# Revit family: Skylight_SF_AmericanSkylites
name_source: partatom
category: Windows
units: mm (PartAtom-declared; Revit-internal decimal feet)

## family parameters
Always vertical = No
Cut with Voids When Loaded = No
Host = Roof
Room Calculation Point = No
Shared = No

## types (61) — shared parameters
Assembly Code = B3020110
Building Codes = http://www.americanskylites.com
Construction Details = http://www.arcat.com
E283_Air Infiltration = 898560.00 psf
E330_Uniform Load_Neg = 10800000.00 psf
E330_Uniform Load_Pos = 9936000.00 psf
E547_E331_Water Penetration = 2160000.00 psf
ENERGYSTAR Qualified = Non-Compliant
Expected Lifespan (Years) = 20
Flange Extension = 0' - 3"
Flashing Clearance = 0' - 0 3/8"
Green Building-LEED = http://www.arcat.com
Installation Phase = Roof Enclosure
Insulation Thickness = 0' - 0 3/4"
Keynote = 08620
Maintenance Schedule (Months) = 12
Manufacturer = American Skylights, Inc
Manufacturer Fax = 817-633-4616
Manufacturer Website = http://www.americanskylites.com
Operation = Fixed
Product Data = http://www.arcat.com
Product Properties = http://www.arcat.com
Sales Information = http://www.americanskylites.com
Send Message = http://admin.arcat.com
SpecWizard = http://www.arcat.com
Specification = http://www.arcat.com
Warranty Duration (Years) = 10
zero-valued in all types: Cost

## per-type parameters (varying)
| type | Description | Dome Type | Frame Material | Inner Dome Material | Insulation Material | IsInsulated | Model | Outer Dome Material | SHGC | Type Comments | U_Factor | Unit Height |
| Miami-Dade Approved Thermally Broken Curb Mount - Glazing and size as Specified | CM4669 Single Dome Skylight - Glazing As Specified | Glazing_Double Dome : As Specified | Aluminum 0.060" - Finish as Specified | None | Wood Materials - Pine | No | CM4669 | Acrylic - Clear | 1.1155 |  | 0.8 | 0' - 9" |
| Thermally Broken Fall Protection - Glazing and size as Specified | Thermally Broken Double Dome Skylight - Size and Glazing As Specified | Glazing_Double Dome : As Specified | Aluminum 0.060" - Finish as Specified | Polycarbonate - Clear | Wood Materials - Pine | Yes | TCM-FG | Polycarbonate - Clear | 1.023 | Report# CCLI-00-109 | 0.5 | 1' - 0" |
| Thermally Broken Venting Flat - Glazing and size as Specified | Thermally Broken Venting Flat Skylight - Size and Glazing As Specified | Glazing_Double Dome : As Specified | Aluminum 0.060" - Finish as Specified | None | Wood Materials - Pine | Yes | GTVCM | Twinwall Polycarbonate - Clear | 1.1155 |  | 0.8 | 1' - 0" |
| Thermally Broken Venting Double Dome - Glazing and size as Specified | Thermally Broken Venting Double Dome Skylight - Size and Glazing As Specified | Glazing_Double Dome : As Specified | Aluminum 0.060" - Finish as Specified | Acrylic - Clear | Wood Materials - Pine | Yes | TVCM | Acrylic - Clear | 1.023 |  | 0.5 | 1' - 0" |
| Thermally Broken Venting Dome - Glazing and size as Specified | Thermally Broken Venting Dome Skylight - Size and Glazing As Specified | Glazing_Double Dome : As Specified | Aluminum 0.060" - Finish as Specified | None | Wood Materials - Pine | Yes | TVCM | Acrylic - Clear | 1.1155 |  | 0.8 | 1' - 0" |
| Thermally Broken 40 Deg Double Pyramid - Glazing and size as Specified | Thermally Broken 40 Deg Double Pyramid Skylight - Size and Glazing As Specified | Glazing_Double Dome : As Specified | Aluminum 0.060" - Finish as Specified | Acrylic - Clear | Wood Materials - Pine | Yes | TCM-PYR | Acrylic - Clear | 1.023 |  | 0.5 | 1' - 0" |
| Thermally Broken 40 Deg Pyramid - Glazing and size as Specified | Thermally Broken 40 Deg Pyramid Skylight - Size and Glazing As Specified | Glazing_Double Dome : As Specified | Aluminum 0.060" - Finish as Specified | None | Wood Materials - Pine | Yes | TCM-PYR | Acrylic - Clear | 1.1155 |  | 0.8 | 1' - 0" |
| Thermally Broken 30 Deg Double Pyramid - Glazing and size as Specified | Thermally Broken 30 Deg Double Pyramid Skylight - Size and Glazing As Specified | Glazing_Double Dome : As Specified | Aluminum 0.060" - Finish as Specified | Acrylic - Clear | Wood Materials - Pine | Yes | TCM-PYR | Acrylic - Clear | 1.023 |  | 0.5 | 1' - 0" |
| Thermally Broken 30 Deg Pyramid - Glazing and size as Specified | Thermally Broken 30 Deg Pyramid Skylight - Size and Glazing As Specified | Glazing_Double Dome : As Specified | Aluminum 0.060" - Finish as Specified | None | Wood Materials - Pine | Yes | TCM-PYR | Acrylic - Clear | 1.1155 |  | 0.8 | 1' - 0" |
| Thermally Broken 22 Deg Double Pyramid - Glazing and size as Specified | Thermally Broken 22 Deg Double Pyramid Skylight - Size and Glazing As Specified | Glazing_Double Dome : As Specified | Aluminum 0.060" - Finish as Specified | Acrylic - Clear | Wood Materials - Pine | Yes | TCM-PYR | Acrylic - Clear | 1.023 |  | 0.5 | 1' - 0" |
| Thermally Broken 22 Deg Pyramid - Glazing and size as Specified | Thermally Broken 22 Deg Pyramid Skylight - Size and Glazing As Specified | Glazing_Double Dome : As Specified | Aluminum 0.060" - Finish as Specified | None | Wood Materials - Pine | Yes | TCM-PYR | Acrylic - Clear | 1.1155 |  | 0.8 | 1' - 0" |
| Thermally Broken Flat - Glazing and size as Specified | Thermally Broken Flat Skylight - Size and Glazing As Specified | Glazing_Dome : As Specified | Aluminum 0.060" - Mill Finish | None | Insulation_Polyisocyanurate | Yes | TCM | Twinwall Polycarbonate - Clear | 1.1155 |  | 0.8 | 1' - 0" |
| Thermally Broken Double Dome - Glazing and size as Specified | Thermally Broken Double Dome Skylight - Size and Glazing As Specified | Glazing_Double Dome : As Specified | Aluminum 0.060" - Finish as Specified | Acrylic - Clear | Wood Materials - Pine | Yes | TCM | Acrylic - Clear | 1.023 |  | 0.5 | 1' - 0" |
| Thermally Broken Dome - Glazing and size as Specified | Thermally Broken Dome Skylight - Size and Glazing As Specified | Glazing_Double Dome : As Specified | Aluminum 0.060" - Finish as Specified | None | Wood Materials - Pine | Yes | TCM | Acrylic - Clear | 1.1155 |  | 0.8 | 1' - 0" |
| 40 Deg Double Pyramid - Glazing and size as Specified | 40 Deg Double Pyramid Skylight - Size and Glazing As Specified | Glazing_Double Dome : As Specified | Aluminum 0.060" - Finish as Specified | Acrylic - Clear | Wood Materials - Pine | Yes | CM-PYR | Acrylic - Clear | 1.023 |  | 0.5 | 1' - 0" |
| 40 Deg Pyramid - Glazing and size as Specified | 40 Deg Pyramid Skylight - Size and Glazing As Specified | Glazing_Double Dome : As Specified | Aluminum 0.060" - Finish as Specified | None | Wood Materials - Pine | Yes | CM-PYR | Acrylic - Clear | 1.1155 |  | 0.8 | 1' - 0" |
| 30 Deg Double Pyramid - Glazing and size as Specified | 30 Deg Double Pyramid Skylight - Size and Glazing As Specified | Glazing_Double Dome : As Specified | Aluminum 0.060" - Finish as Specified | Acrylic - Clear | Wood Materials - Pine | Yes | CM-PYR | Acrylic - Clear | 1.023 |  | 0.5 | 1' - 0" |
| 30 Deg Pyramid - Glazing and size as Specified | 30 Deg Pyramid Skylight - Size and Glazing As Specified | Glazing_Double Dome : As Specified | Aluminum 0.060" - Finish as Specified | None | Wood Materials - Pine | Yes | CM-PYR | Acrylic - Clear | 1.1155 |  | 0.8 | 1' - 0" |
| 22 Deg Double Pyramid - Glazing and size as Specified | 22 Deg Double Pyramid Skylight - Size and Glazing As Specified | Glazing_Double Dome : As Specified | Aluminum 0.060" - Finish as Specified | Acrylic - Clear | Wood Materials - Pine | Yes | CM-PYR | Acrylic - Clear | 1.023 |  | 0.5 | 1' - 0" |
| 22 Deg Pyramid - Glazing and size as Specified | 22 Deg Pyramid Skylight - Size and Glazing As Specified | Glazing_Double Dome : As Specified | Aluminum 0.060" - Finish as Specified | None | Wood Materials - Pine | Yes | CM-PYR | Acrylic - Clear | 1.1155 |  | 0.8 | 1' - 0" |
| Flat - Glazing and size as Specified | Flat Skylight - Size and Glazing As Specified | Glazing_Double Dome : As Specified | Aluminum 0.060" - Finish as Specified | None | Wood Materials - Pine | Yes | CM | Twinwall Polycarbonate - Clear | 1.1155 |  | 0.8 | 1' - 0" |
| Double Dome - Glazing and size as Specified | Double Dome Skylight - Size and Glazing As Specified | Glazing_Double Dome : As Specified | Aluminum 0.060" - Finish as Specified | Acrylic - Clear | Wood Materials - Pine | Yes | CM | Acrylic - Clear | 1.023 |  | 0.5 | 1' - 0" |
| CM7090  - Single Dome - Glazing as Specified | CM7090 Single Dome Skylight - Glazing As Specified | Glazing_Double Dome : As Specified | Aluminum 0.060" - Finish as Specified | None | Wood Materials - Pine | No | CM7090 | Acrylic - Clear | 1.1155 |  | 0.8 | 0' - 5 1/4" |
| CM5789  - Single Dome - Glazing as Specified | CM5789 Single Dome Skylight - Glazing As Specified | Glazing_Double Dome : As Specified | Aluminum 0.060" - Finish as Specified | None | Wood Materials - Pine | Yes | CM5789 | Acrylic - Clear | 1.1155 |  | 0.8 | 1' - 0" |
| CM5769  - Single Dome - Glazing as Specified | CM5769 Single Dome Skylight - Glazing As Specified | Glazing_Double Dome : As Specified | Aluminum 0.060" - Finish as Specified | None | Wood Materials - Pine | Yes | CM5769 | Acrylic - Clear | 1.1155 |  | 0.8 | 1' - 0" |
| CM4689  - Single Dome - Glazing as Specified | CM4689 Single Dome Skylight - Glazing As Specified | Glazing_Double Dome : As Specified | Aluminum 0.060" - Finish as Specified | None | Wood Materials - Pine | Yes | CM4689 | Acrylic - Clear | 1.1155 |  | 0.8 | 1' - 0" |
| CM4669  - Single Dome - Glazing as Specified | CM4669 Single Dome Skylight - Glazing As Specified | Glazing_Double Dome : As Specified | Aluminum 0.060" - Finish as Specified | None | Insulation_Polyisocyanurate | No | CM4669 | Acrylic - Clear | 1.1155 |  | 0.8 | 0' - 9" |
| CM3775  - Single Dome - Glazing as Specified | CM3775 Single Dome Skylight - Glazing As Specified | Glazing_Double Dome : As Specified | Aluminum 0.060" - Finish as Specified | None | Wood Materials - Pine | Yes | CM3775 | Acrylic - Clear | 1.1155 |  | 0.8 | 1' - 0" |
| CM3357  - Single Dome - Glazing as Specified | CM3357 Single Dome Skylight - Glazing As Specified | Glazing_Double Dome : As Specified | Aluminum 0.060" - Finish as Specified | None | Wood Materials - Pine | Yes | CM3357 | Acrylic - Clear | 1.1155 |  | 0.8 | 1' - 0" |
| CM3345  - Single Dome - Glazing as Specified | CM3345 Single Dome Skylight - Glazing As Specified | Glazing_Double Dome : As Specified | Aluminum 0.060" - Finish as Specified | None | Wood Materials - Pine | Yes | CM3345 | Acrylic - Clear | 1.1155 |  | 0.8 | 1' - 0" |
| CM3089  - Single Dome - Glazing as Specified | CM3089 Single Dome Skylight - Glazing As Specified | Glazing_Double Dome : As Specified | Aluminum 0.060" - Finish as Specified | None | Wood Materials - Pine | Yes | CM3089 | Acrylic - Clear | 1.1155 |  | 0.8 | 1' - 0" |
| CM3069  - Single Dome - Glazing as Specified | CM3069 Single Dome Skylight - Glazing As Specified | Glazing_Double Dome : As Specified | Aluminum 0.060" - Finish as Specified | None | Wood Materials - Pine | Yes | CM3069 | Acrylic - Clear | 1.1155 |  | 0.8 | 1' - 0" |
| CM3046  - Single Dome - Glazing as Specified | CM3046 Single Dome Skylight - Glazing As Specified | Glazing_Double Dome : As Specified | Aluminum 0.060" - Finish as Specified | None | Wood Materials - Pine | Yes | CM3046 | Acrylic - Clear | 1.1155 |  | 0.8 | 1' - 0" |
| CM2290  - Single Dome - Glazing as Specified | CM2290 Single Dome Skylight - Glazing As Specified | Glazing_Double Dome : As Specified | Aluminum 0.060" - Finish as Specified | None | Wood Materials - Pine | Yes | CM2290 | Acrylic - Clear | 1.1155 |  | 0.8 | 1' - 0" |
| CM2270  - Single Dome - Glazing as Specified | CM2270 Single Dome Skylight - Glazing As Specified | Glazing_Double Dome : As Specified | Aluminum 0.060" - Finish as Specified | None | Wood Materials - Pine | Yes | CM2270 | Acrylic - Clear | 1.1155 |  | 0.8 | 1' - 0" |
| CM2246  - Single Dome - Glazing as Specified | CM2246 Single Dome Skylight - Glazing As Specified | Glazing_Double Dome : As Specified | Aluminum 0.060" - Finish as Specified | None | Wood Materials - Pine | Yes | CM2246 | Acrylic - Clear | 1.1155 |  | 0.8 | 1' - 0" |
| CM2237  - Single Dome - Glazing as Specified | CM2237 Single Dome Skylight - Glazing As Specified | Glazing_Double Dome : As Specified | Aluminum 0.060" - Finish as Specified | None | Wood Materials - Pine | Yes | CM2237 | Acrylic - Clear | 1.1155 |  | 0.8 | 1' - 0" |
| CM2230  - Single Dome - Glazing as Specified | CM2230 Single Dome Skylight - Glazing As Specified | Glazing_Double Dome : As Specified | Aluminum 0.060" - Finish as Specified | None | Wood Materials - Pine | Yes | CM2230 | Acrylic - Clear | 1.1155 |  | 0.8 | 1' - 0" |
| CM2193  - Single Dome - Glazing as Specified | CM2193 Single Dome Skylight - Glazing As Specified | Glazing_Double Dome : As Specified | Aluminum 0.060" - Finish as Specified | None | Wood Materials - Pine | Yes | CM2193 | Acrylic - Clear | 1.1155 |  | 0.8 | 1' - 0" |
| CM2169  - Single Dome - Glazing as Specified | CM2169 Single Dome Skylight - Glazing As Specified | Glazing_Double Dome : As Specified | Aluminum 0.060" - Finish as Specified | None | Wood Materials - Pine | Yes | CM2169 | Acrylic - Clear | 1.1155 |  | 0.8 | 1' - 0" |
| CM2157  - Single Dome - Glazing as Specified | CM2157 Single Dome Skylight - Glazing As Specified | Glazing_Double Dome : As Specified | Aluminum 0.060" - Finish as Specified | None | Wood Materials - Pine | Yes | CM2157 | Acrylic - Clear | 1.1155 |  | 0.8 | 1' - 0" |
| CM2145  - Single Dome - Glazing as Specified | CM2145 Single Dome Skylight - Glazing As Specified | Glazing_Double Dome : As Specified | Aluminum 0.060" - Finish as Specified | None | Wood Materials - Pine | Yes | CM2145 | Acrylic - Clear | 1.1155 |  | 0.8 | 1' - 0" |
| CM2133  - Single Dome - Glazing as Specified | CM2133 Single Dome Skylight - Glazing As Specified | Glazing_Double Dome : As Specified | Aluminum 0.060" - Finish as Specified | None | Wood Materials - Pine | Yes | CM2133 | Acrylic - Clear | 1.1155 |  | 0.8 | 1' - 0" |
| CM1446  - Single Dome - Glazing as Specified | CM1446 Single Dome Skylight - Glazing As Specified | Glazing_Double Dome : As Specified | Aluminum 0.060" - Finish as Specified | None | Wood Materials - Pine | Yes | CM1446 | Acrylic - Clear | 1.1155 |  | 0.8 | 1' - 0" |
| CM1422  - Single Dome - Glazing as Specified | CM1422 Single Dome Skylight - Glazing As Specified | Glazing_Double Dome : As Specified | Aluminum 0.060" - Finish as Specified | None | Wood Materials - Pine | Yes | CM1422 | Acrylic - Clear | 1.1155 |  | 0.8 | 1' - 0" |
| CM9393  - Single Dome - Glazing as Specified | CM9393 Single Dome Skylight - Glazing As Specified | Glazing_Double Dome : As Specified | Aluminum 0.060" - Finish as Specified | None | Wood Materials - Pine | Yes | CM9393 | Acrylic - Clear | 1.1155 |  | 0.8 | 1' - 0" |
| CM8989  - Single Dome - Glazing as Specified | CM8989 Single Dome Skylight - Glazing As Specified | Glazing_Double Dome : As Specified | Aluminum 0.060" - Finish as Specified | None | Wood Materials - Pine | Yes | CM8989 | Acrylic - Clear | 1.1155 |  | 0.8 | 1' - 0" |
| CM8080  - Single Dome - Glazing as Specified | CM8080 Single Dome Skylight - Glazing As Specified | Glazing_Double Dome : As Specified | Aluminum 0.060" - Finish as Specified | None | Wood Materials - Pine | Yes | CM8080 | Acrylic - Clear | 1.1155 |  | 0.8 | 1' - 0" |
| CM7070  - Single Dome - Glazing as Specified | CM7070 Single Dome Skylight - Glazing As Specified | Glazing_Double Dome : As Specified | Aluminum 0.060" - Finish as Specified | None | Wood Materials - Pine | Yes | CM7070 | Acrylic - Clear | 1.1155 |  | 0.8 | 1' - 0" |
| CM6060  - Single Dome - Glazing as Specified | CM6060 Single Dome Skylight - Glazing As Specified | Glazing_Double Dome : As Specified | Aluminum 0.060" - Finish as Specified | None | Wood Materials - Pine | Yes | CM6060 | Acrylic - Clear | 1.1155 |  | 0.8 | 1' - 0" |
| CM5757  - Single Dome - Glazing as Specified | CM5757 Single Dome Skylight - Glazing As Specified | Glazing_Double Dome : As Specified | Aluminum 0.060" - Finish as Specified | None | Wood Materials - Pine | Yes | CM5757 | Acrylic - Clear | 1.1155 |  | 0.8 | 1' - 0" |
| CM5555  - Single Dome - Glazing as Specified | CM5555 Single Dome Skylight - Glazing As Specified | Glazing_Double Dome : As Specified | Aluminum 0.060" - Finish as Specified | None | Wood Materials - Pine | Yes | CM5555 | Acrylic - Clear | 1.1155 |  | 0.8 | 1' - 0" |
| CM4646  - Single Dome - Glazing as Specified | CM4646 Single Dome Skylight - Glazing As Specified | Glazing_Double Dome : As Specified | Aluminum 0.060" - Finish as Specified | None | Wood Materials - Pine | Yes | CM4646 | Acrylic - Clear | 1.1155 |  | 0.8 | 1' - 0" |
| CM4545  - Single Dome - Glazing as Specified | CM4545 Single Dome Skylight - Glazing As Specified | Glazing_Double Dome : As Specified | Aluminum 0.060" - Finish as Specified | None | Wood Materials - Pine | Yes | CM4545 | Acrylic - Clear | 1.1155 |  | 0.8 | 1' - 0" |
| CM3636  - Single Dome - Glazing as Specified | CM3636 Single Dome Skylight - Glazing As Specified | Glazing_Double Dome : As Specified | Aluminum 0.060" - Finish as Specified | None | Wood Materials - Pine | Yes | CM3636 | Acrylic - Clear | 1.1155 |  | 0.8 | 1' - 0" |
| CM3333  - Single Dome - Glazing as Specified | CM3333 Single Dome Skylight - Glazing As Specified | Glazing_Double Dome : As Specified | Aluminum 0.060" - Finish as Specified | None | Wood Materials - Pine | Yes | CM3333 | Acrylic - Clear | 1.1155 |  | 0.8 | 1' - 0" |
| CM3030  - Single Dome - Glazing as Specified | CM3030 Single Dome Skylight - Glazing As Specified | Glazing_Double Dome : As Specified | Aluminum 0.060" - Finish as Specified | None | Wood Materials - Pine | Yes | CM3030 | Acrylic - Clear | 1.1155 |  | 0.8 | 1' - 0" |
| CM2222  - Single Dome - Glazing as Specified | CM2222 Single Dome Skylight - Glazing As Specified | Glazing_Double Dome : As Specified | Aluminum 0.060" - Finish as Specified | None | Wood Materials - Pine | Yes | CM2222 | Acrylic - Clear | 1.1155 |  | 0.8 | 1' - 0" |
| CM2121  - Single Dome - Glazing as Specified | CM2121 Single Dome Skylight - Glazing As Specified | Glazing_Double Dome : As Specified | Aluminum 0.060" - Finish as Specified | None | Wood Materials - Pine | Yes | CM2121 | Acrylic - Clear | 1.1155 |  | 0.8 | 1' - 0" |
| CM1919  - Single Dome - Glazing as Specified | CM1919 Single Dome Skylight - Glazing As Specified | Glazing_Double Dome : As Specified | Aluminum 0.060" - Finish as Specified | None | Wood Materials - Pine | Yes | CM1919 | Acrylic - Clear | 1.1155 |  | 0.8 | 1' - 0" |
| CM1414  - Single Dome - Glazing as Specified | CM1414 Single Dome Skylight - Glazing As Specified | Glazing_Double Dome : As Specified | Aluminum 0.060" - Finish as Specified | None | Wood Materials - Pine | Yes | CM1414 | Acrylic - Clear | 1.1155 |  | 0.8 | 1' - 0" |

## geometry (parser evidence)
native form markers: Blend x85, Sweep x15
no freeform markers — native parametric forms only
